# Revit family: Haworth_Maari_Stool_StandardBack_EU_PRELIMINARY
name_source: partatom
category: Furniture
units: mm (PartAtom-declared; Revit-internal decimal feet)

## family parameters
Always vertical = Yes
Cut with Voids When Loaded = No
OmniClass Number = 23.40.70.14.64.21
OmniClass Title = Systems Furniture
Room Calculation Point = No
Shared = No
Work Plane-Based = No

## types (3) — shared parameters
Actual Depth = 58 cm
Actual Height = 110 cm
Actual Width = 58 cm
Arm Cap Finish = Haworth _ Polymer _ Undecided
Assembly Code = E2020200
Description = Haworth - Maari - Stool - Standard Back
Manufacturer = Haworth
Model = SEMIGXB7
Revision Number = 2
Size = Verify Final Dim. w/ Haworth
URL = https://www.haworth.com
URL - Product = https://www.haworth.com
Warranty = http://www.haworth.com

## per-type parameters (varying)
| type | Four Legs | Sled Base | Wood Base |
| Sled Base | No | Yes | No |
| Wood Leg | No | No | Yes |
| Four Legs | Yes | No | No |

## geometry (parser evidence)
native form markers: Blend x8, Sweep x7
no freeform markers — native parametric forms only
